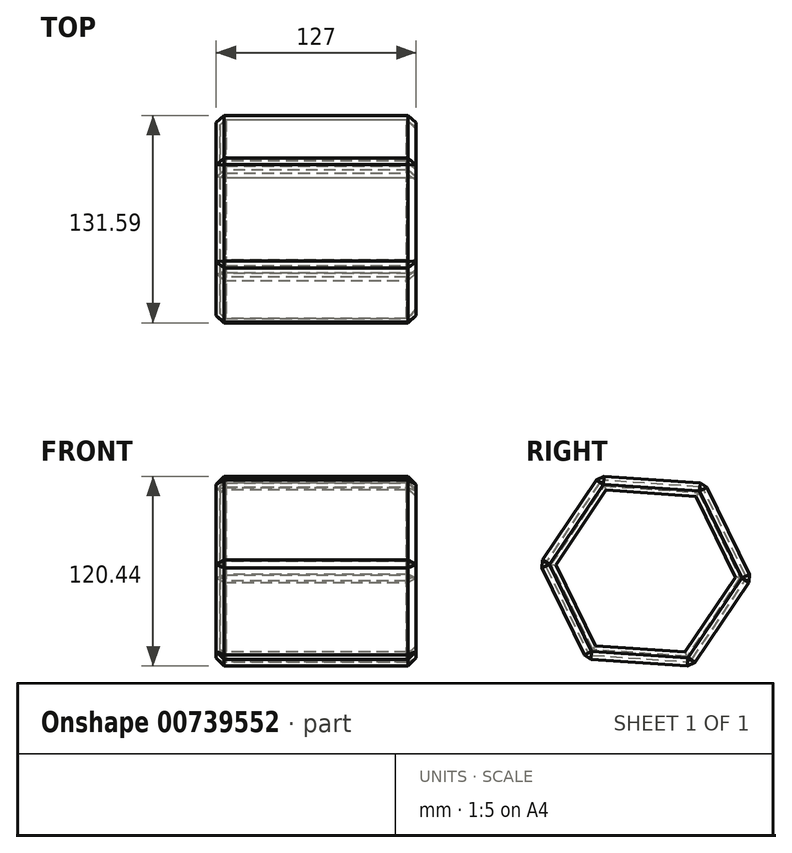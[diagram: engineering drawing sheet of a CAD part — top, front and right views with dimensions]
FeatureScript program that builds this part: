
annotation { "Feature Type Name" : "Feature", "Feature Type Description" : "" }
export const myFeature = defineFeature(function(context is Context, id is Id, definition is map)
    precondition{}
    {
        {
            var Q0;
            Q0=qCreatedBy(makeId("Right.planeOp"),FACE);
            var sketch = newSketch(context, id + "F0", { "sketchPlane" : qUnion([Q0])});
            skCircle(sketch, "E0.cCircle", {"center": v(-103.1, 65.38) * mm, "radius": 58.23 * mm, "construction": true});
            skLineSegment(sketch, "E0.0", {"start": v(-36.02, 60.72) * mm, "end": v(-73.6, 4.95) * mm});
            skLineSegment(sketch, "E0.1", {"start": v(-73.6, 4.95) * mm, "end": v(-140.68, 9.61) * mm});
            skLineSegment(sketch, "E0.2", {"start": v(-140.68, 9.61) * mm, "end": v(-170.19, 70.04) * mm});
            skLineSegment(sketch, "E0.3", {"start": v(-170.19, 70.04) * mm, "end": v(-132.61, 125.8) * mm});
            skLineSegment(sketch, "E0.4", {"start": v(-132.61, 125.8) * mm, "end": v(-65.53, 121.14) * mm});
            skLineSegment(sketch, "E0.5", {"start": v(-65.53, 121.14) * mm, "end": v(-36.02, 60.72) * mm});
            skPoint(sketch, "E0.0.midPoint", {"position": v(-54.81, 32.84) * mm});
            skSolve(sketch);
        }
        {
            var Q0;
            Q0=makeQuery(id+"F0.imprint","IMPRINT",FACE,{"disambiguationData":[TD([[makeQuery(id+"F0.imprint","IMPRINT",EDGE,{"derivedFrom":sQuery(id+"F0.wireOp",EDGE,"E0.0")}),-1.0]])]});
            extrude(context, id + "F1", {"entities" : qUnion([Q0]), "depth" : 127 * mm, "offsetDistance" : 25.4 * mm});
        }
        {
            var Q0;
            Q0=makeQuery(id+"F1.opExtrude","CAP_EDGE",EDGE,{"disambiguationData":[OSD([sQuery(id+"F0.wireOp",EDGE,"E0.4")])],"isStart":false});
            var Q1;
            Q1=makeQuery(id+"F1.opExtrude","CAP_EDGE",EDGE,{"disambiguationData":[OSD([sQuery(id+"F0.wireOp",EDGE,"E0.5")])],"isStart":false});
            var Q2;
            Q2=makeQuery(id+"F1.opExtrude","CAP_EDGE",EDGE,{"disambiguationData":[OSD([sQuery(id+"F0.wireOp",EDGE,"E0.0")])],"isStart":false});
            var Q3;
            Q3=makeQuery(id+"F1.opExtrude","CAP_EDGE",EDGE,{"disambiguationData":[OSD([sQuery(id+"F0.wireOp",EDGE,"E0.1")])],"isStart":false});
            var Q4;
            Q4=makeQuery(id+"F1.opExtrude","CAP_EDGE",EDGE,{"disambiguationData":[OSD([sQuery(id+"F0.wireOp",EDGE,"E0.2")])],"isStart":false});
            var Q5;
            Q5=makeQuery(id+"F1.opExtrude","CAP_EDGE",EDGE,{"disambiguationData":[OSD([sQuery(id+"F0.wireOp",EDGE,"E0.3")])],"isStart":false});
            var Q6;
            Q6=makeQuery(id+"F1.opExtrude","CAP_EDGE",EDGE,{"disambiguationData":[OSD([sQuery(id+"F0.wireOp",EDGE,"E0.3")])],"isStart":true});
            var Q7;
            Q7=makeQuery(id+"F1.opExtrude","CAP_EDGE",EDGE,{"disambiguationData":[OSD([sQuery(id+"F0.wireOp",EDGE,"E0.4")])],"isStart":true});
            var Q8;
            Q8=makeQuery(id+"F1.opExtrude","CAP_EDGE",EDGE,{"disambiguationData":[OSD([sQuery(id+"F0.wireOp",EDGE,"E0.5")])],"isStart":true});
            var Q9;
            Q9=makeQuery(id+"F1.opExtrude","CAP_EDGE",EDGE,{"disambiguationData":[OSD([sQuery(id+"F0.wireOp",EDGE,"E0.2")])],"isStart":true});
            var Q10;
            Q10=makeQuery(id+"F1.opExtrude","CAP_EDGE",EDGE,{"disambiguationData":[OSD([sQuery(id+"F0.wireOp",EDGE,"E0.1")])],"isStart":true});
            var Q11;
            Q11=makeQuery(id+"F1.opExtrude","CAP_EDGE",EDGE,{"disambiguationData":[OSD([sQuery(id+"F0.wireOp",EDGE,"E0.0")])],"isStart":true});
            var Q12;
            Q12=makeQuery(id+"F1.opExtrude","SWEPT_EDGE",EDGE,{"disambiguationData":[OSD([sQuery(id+"F0.wireOp",EDGE,"E0.0"),sQuery(id+"F0.wireOp",EDGE,"E0.1")])]});
            var Q13;
            Q13=makeQuery(id+"F1.opExtrude","SWEPT_EDGE",EDGE,{"disambiguationData":[OSD([sQuery(id+"F0.wireOp",EDGE,"E0.1"),sQuery(id+"F0.wireOp",EDGE,"E0.2")])]});
            var Q14;
            Q14=makeQuery(id+"F1.opExtrude","SWEPT_EDGE",EDGE,{"disambiguationData":[OSD([sQuery(id+"F0.wireOp",EDGE,"E0.2"),sQuery(id+"F0.wireOp",EDGE,"E0.3")])]});
            var Q15;
            Q15=makeQuery(id+"F1.opExtrude","SWEPT_EDGE",EDGE,{"disambiguationData":[OSD([sQuery(id+"F0.wireOp",EDGE,"E0.3"),sQuery(id+"F0.wireOp",EDGE,"E0.4")])]});
            var Q16;
            Q16=makeQuery(id+"F1.opExtrude","SWEPT_EDGE",EDGE,{"disambiguationData":[OSD([sQuery(id+"F0.wireOp",EDGE,"E0.0"),sQuery(id+"F0.wireOp",EDGE,"E0.5")])]});
            var Q17;
            Q17=makeQuery(id+"F1.opExtrude","SWEPT_EDGE",EDGE,{"disambiguationData":[OSD([sQuery(id+"F0.wireOp",EDGE,"E0.4"),sQuery(id+"F0.wireOp",EDGE,"E0.5")])]});
            chamfer(context, id + "F2", {"entities" : qUnion([Q0, Q1, Q2, Q3, Q4, Q5, Q6, Q7, Q8, Q9, Q10, Q11, Q12, Q13, Q14, Q15, Q16, Q17]), "width" : 5.08 * mm, "tangentPropagation" : true});
        }
        {
            var Q0;
            Q0=makeQuery(id+"F1.opExtrude","CAP_FACE",FACE,{"disambiguationData":[OSD([sQuery(id+"F0.wireOp",EDGE,"E0.0"),sQuery(id+"F0.wireOp",EDGE,"E0.1"),sQuery(id+"F0.wireOp",EDGE,"E0.2"),sQuery(id+"F0.wireOp",EDGE,"E0.3"),sQuery(id+"F0.wireOp",EDGE,"E0.4"),sQuery(id+"F0.wireOp",EDGE,"E0.5")])],"isStart":false});
            shell(context, id + "F3", {"entities" : qUnion([Q0]), "thickness" : 2.54 * mm});
        }
    });
